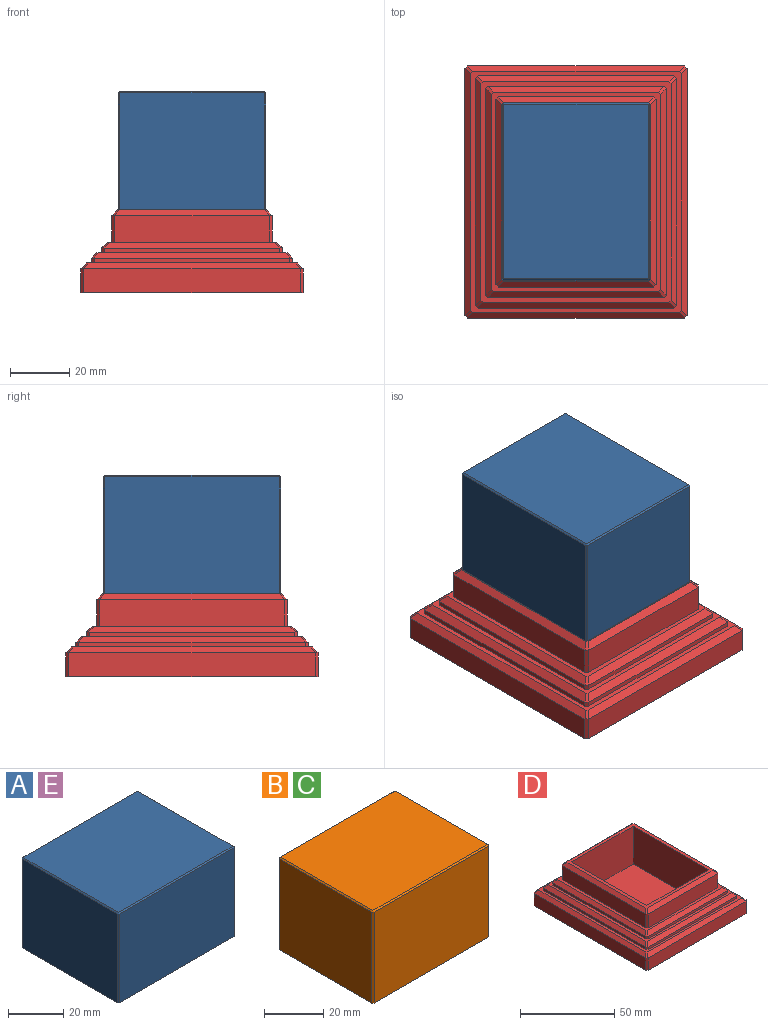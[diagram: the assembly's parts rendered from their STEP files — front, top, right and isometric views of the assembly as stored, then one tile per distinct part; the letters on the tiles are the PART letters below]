
ASSEMBLY  parts=5 mates=4
PART A: 23 faces, bbox 60x50x40 mm
  f0: plane 60x50mm, normal (0,0,-1), area 423.5mm2, adj f1,f2,f3,f4,f6,f7,f8,f9
  f1: plane 49x39.5mm, normal (1,0,0), area 1935.5mm2, adj f0,f13,f19,f22
  f2: plane 59x39.5mm, normal (0,1,0), area 2330.5mm2, adj f0,f16,f20,f22
  f3: plane 49x39.5mm, normal (-1,0,0), area 1935.5mm2, adj f0,f11,f15,f16
  f4: plane 59x39.5mm, normal (0,-1,0), area 2330.5mm2, adj f0,f11,f13,f14
  f5: plane 59x49mm, normal (0,0,1), area 2891mm2, adj f14,f15,f19,f20
  f6: plane 46x38mm, normal (-1,0,0), area 1748mm2, adj f0,f7,f9,f10
  f7: plane 56x38mm, normal (0,-1,0), area 2128mm2, adj f0,f6,f8,f10
  f8: plane 46x38mm, normal (1,0,0), area 1748mm2, adj f0,f7,f9,f10
  f9: plane 56x38mm, normal (0,1,0), area 2128mm2, adj f0,f6,f8,f10
  f10: plane 56x46mm, normal (0,0,-1), area 2576mm2, adj f6,f7,f8,f9
  f11: plane 39.5x0.5mm, normal (-0.71,-0.71,0), area 27.9mm2, adj f0,f3,f4,f12
  f12: plane 0.5x0.5mm, normal (-0.58,-0.58,0.58), area 0.2mm2, adj f11,f14,f15
  f13: plane 39.5x0.5mm, normal (0.71,-0.71,0), area 27.9mm2, adj f0,f1,f4,f17
  f14: plane 59x0.5mm, normal (0,-0.71,0.71), area 41.7mm2, adj f4,f5,f12,f17
  f15: plane 49x0.5mm, normal (-0.71,0,0.71), area 34.6mm2, adj f3,f5,f12,f18
  f16: plane 39.5x0.5mm, normal (-0.71,0.71,0), area 27.9mm2, adj f0,f2,f3,f18
  f17: plane 0.5x0.5mm, normal (0.58,-0.58,0.58), area 0.2mm2, adj f13,f14,f19
  f18: plane 0.5x0.5mm, normal (-0.58,0.58,0.58), area 0.2mm2, adj f15,f16,f20
  f19: plane 49x0.5mm, normal (0.71,0,0.71), area 34.6mm2, adj f1,f5,f17,f21
  f20: plane 59x0.5mm, normal (0,0.71,0.71), area 41.7mm2, adj f2,f5,f18,f21
  f21: plane 0.5x0.5mm, normal (0.58,0.58,0.58), area 0.2mm2, adj f19,f20,f22
  f22: plane 39.5x0.5mm, normal (0.71,0.71,0), area 27.9mm2, adj f0,f1,f2,f21
PART B: 23 faces, bbox 55.5x45x38 mm
  f0: plane 55.5x45mm, normal (0,0,-1), area 385.5mm2, adj f1,f2,f3,f4,f6,f7,f8,f9
  f1: plane 44x37.5mm, normal (1,0,0), area 1650mm2, adj f0,f11,f13,f14
  f2: plane 54.5x37.5mm, normal (0,1,0), area 2043.7mm2, adj f0,f13,f19,f22
  f3: plane 44x37.5mm, normal (-1,0,0), area 1650mm2, adj f0,f16,f20,f22
  f4: plane 54.5x37.5mm, normal (0,-1,0), area 2043.7mm2, adj f0,f11,f15,f16
  f5: plane 54.5x44mm, normal (0,0,1), area 2398mm2, adj f14,f15,f19,f20
  f6: plane 41x36mm, normal (-1,0,0), area 1476mm2, adj f0,f7,f9,f10
  f7: plane 51.5x36mm, normal (0,-1,0), area 1854mm2, adj f0,f6,f8,f10
  f8: plane 41x36mm, normal (1,0,0), area 1476mm2, adj f0,f7,f9,f10
  f9: plane 51.5x36mm, normal (0,1,0), area 1854mm2, adj f0,f6,f8,f10
  f10: plane 51.5x41mm, normal (0,0,-1), area 2111.5mm2, adj f6,f7,f8,f9
  f11: plane 37.5x0.5mm, normal (0.71,-0.71,0), area 26.5mm2, adj f0,f1,f4,f12
  f12: plane 0.5x0.5mm, normal (0.58,-0.58,0.58), area 0.2mm2, adj f11,f14,f15
  f13: plane 37.5x0.5mm, normal (0.71,0.71,0), area 26.5mm2, adj f0,f1,f2,f17
  f14: plane 44x0.5mm, normal (0.71,0,0.71), area 31.1mm2, adj f1,f5,f12,f17
  f15: plane 54.5x0.5mm, normal (0,-0.71,0.71), area 38.5mm2, adj f4,f5,f12,f18
  f16: plane 37.5x0.5mm, normal (-0.71,-0.71,0), area 26.5mm2, adj f0,f3,f4,f18
  f17: plane 0.5x0.5mm, normal (0.58,0.58,0.58), area 0.2mm2, adj f13,f14,f19
  f18: plane 0.5x0.5mm, normal (-0.58,-0.58,0.58), area 0.2mm2, adj f15,f16,f20
  f19: plane 54.5x0.5mm, normal (0,0.71,0.71), area 38.5mm2, adj f2,f5,f17,f21
  f20: plane 44x0.5mm, normal (-0.71,0,0.71), area 31.1mm2, adj f3,f5,f18,f21
  f21: plane 0.5x0.5mm, normal (-0.58,0.58,0.58), area 0.2mm2, adj f19,f20,f22
  f22: plane 37.5x0.5mm, normal (-0.71,0.71,0), area 26.5mm2, adj f0,f2,f3,f21
PART C: same geometry as B
PART D: 74 faces, bbox 75.2x85.5x28 mm
  f0: plane 46.25x24.5mm, normal (0,-1,0), area 1133.1mm2, adj f1,f2,f24,f25
  f1: plane 56.5x24.5mm, normal (-1,0,0), area 1384.3mm2, adj f0,f3,f24,f25
  f2: plane 56.5x24.5mm, normal (1,0,0), area 1384.3mm2, adj f0,f3,f24,f25
  f3: plane 46.25x24.5mm, normal (0,1,0), area 1133.1mm2, adj f1,f2,f24,f25
  f4: plane 52.25x9mm, normal (0,1,0), area 470.2mm2, adj f17,f26,f50,f58
  f5: plane 59.25x1.5mm, normal (0,1,0), area 88.9mm2, adj f19,f33,f52,f60
  f6: plane 66.25x1.5mm, normal (0,1,0), area 99.4mm2, adj f21,f37,f54,f62
  f7: plane 73.25x8mm, normal (0,1,0), area 586mm2, adj f23,f40,f56,f64
  f8: plane 62.5x9mm, normal (1,0,0), area 562.5mm2, adj f17,f27,f58,f66
  f9: plane 69.5x1.5mm, normal (1,0,0), area 104.3mm2, adj f19,f32,f60,f68
  f10: plane 76.5x1.5mm, normal (1,0,0), area 114.7mm2, adj f21,f36,f62,f70
  f11: plane 83.5x8mm, normal (1,0,0), area 668mm2, adj f23,f38,f64,f72
  f12: plane 62.5x9mm, normal (-1,0,0), area 562.5mm2, adj f17,f28,f42,f50
  f13: plane 69.5x1.5mm, normal (-1,0,0), area 104.3mm2, adj f19,f31,f44,f52
  f14: plane 76.5x1.5mm, normal (-1,0,0), area 114.7mm2, adj f21,f35,f46,f54
  f15: plane 83.5x8mm, normal (-1,0,0), area 668mm2, adj f23,f41,f48,f56
  f16: plane 52.25x9mm, normal (0,-1,0), area 470.2mm2, adj f17,f29,f42,f66
  f17: plane 67.5x57.25mm, normal (0,0,1), area 366.2mm2, adj f4,f8,f12,f16,f30,f31,f32,f33
  f18: plane 59.25x1.5mm, normal (0,-1,0), area 88.9mm2, adj f19,f30,f44,f68
  f19: plane 74.5x64.25mm, normal (0,0,1), area 408.2mm2, adj f5,f9,f13,f18,f34,f35,f36,f37
  f20: plane 66.25x1.5mm, normal (0,-1,0), area 99.4mm2, adj f21,f34,f46,f70
  f21: plane 81.5x71.25mm, normal (0,0,1), area 450.2mm2, adj f6,f10,f14,f20,f38,f39,f40,f41
  f22: plane 73.25x8mm, normal (0,-1,0), area 586mm2, adj f23,f39,f48,f72
  f23: plane 85.5x75.25mm, normal (0,0,-1), area 6431.7mm2, adj f7,f11,f15,f22,f48,f56,f64,f72
  f24: plane 60.5x50.25mm, normal (0,0,1), area 426mm2, adj f0,f1,f2,f3,f26,f27,f28,f29
  f25: plane 56.5x46.25mm, normal (0,0,1), area 2613mm2, adj f0,f1,f2,f3
  f26: plane 52.54x2mm, normal (0,0.71,0.71), area 143.7mm2, adj f4,f24,f50,f51,f58,f59
  f27: plane 62.79x2mm, normal (0.71,0,0.71), area 172.7mm2, adj f8,f24,f58,f59,f66,f67
  f28: plane 62.79x2mm, normal (-0.71,0,0.71), area 172.7mm2, adj f12,f24,f42,f43,f50,f51
  f29: plane 52.54x2mm, normal (0,-0.71,0.71), area 143.7mm2, adj f16,f24,f42,f43,f66,f67
  f30: plane 59.54x2mm, normal (0,-0.71,0.71), area 163.5mm2, adj f17,f18,f44,f45,f68,f69
  f31: plane 69.79x2mm, normal (-0.71,0,0.71), area 192.5mm2, adj f13,f17,f44,f45,f52,f53
  f32: plane 69.79x2mm, normal (0.71,0,0.71), area 192.5mm2, adj f9,f17,f60,f61,f68,f69
  f33: plane 59.54x2mm, normal (0,0.71,0.71), area 163.5mm2, adj f5,f17,f52,f53,f60,f61
  f34: plane 66.54x2mm, normal (0,-0.71,0.71), area 183.3mm2, adj f19,f20,f46,f47,f70,f71
  f35: plane 76.79x2mm, normal (-0.71,0,0.71), area 212.3mm2, adj f14,f19,f46,f47,f54,f55
  f36: plane 76.79x2mm, normal (0.71,0,0.71), area 212.3mm2, adj f10,f19,f62,f63,f70,f71
  f37: plane 66.54x2mm, normal (0,0.71,0.71), area 183.3mm2, adj f6,f19,f54,f55,f62,f63
  f38: plane 83.79x2mm, normal (0.71,0,0.71), area 232.1mm2, adj f11,f21,f64,f65,f72,f73
  f39: plane 73.54x2mm, normal (0,-0.71,0.71), area 203.1mm2, adj f21,f22,f48,f49,f72,f73
  f40: plane 73.54x2mm, normal (0,0.71,0.71), area 203.1mm2, adj f7,f21,f56,f57,f64,f65
  f41: plane 83.79x2mm, normal (-0.71,0,0.71), area 232.1mm2, adj f15,f21,f48,f49,f56,f57
  f42: plane 9.15x1mm, normal (-0.71,-0.71,0), area 12.9mm2, adj f12,f16,f17,f28,f29,f43
  f43: plane 2.56x2.56mm, normal (-0.41,-0.41,0.82), area 3.2mm2, adj f24,f28,f29,f42
  f44: plane 1.65x1mm, normal (-0.71,-0.71,0), area 2.3mm2, adj f13,f18,f19,f30,f31,f45
  f45: plane 2.56x2.56mm, normal (-0.41,-0.41,0.82), area 3.2mm2, adj f17,f30,f31,f44
  f46: plane 1.65x1mm, normal (-0.71,-0.71,0), area 2.3mm2, adj f14,f20,f21,f34,f35,f47
  f47: plane 2.56x2.56mm, normal (-0.41,-0.41,0.82), area 3.2mm2, adj f19,f34,f35,f46
  f48: plane 8.15x1mm, normal (-0.71,-0.71,0), area 11.5mm2, adj f15,f22,f23,f39,f41,f49
  f49: plane 2.56x2.56mm, normal (-0.41,-0.41,0.82), area 3.2mm2, adj f21,f39,f41,f48
  f50: plane 9.15x1mm, normal (-0.71,0.71,0), area 12.9mm2, adj f4,f12,f17,f26,f28,f51
  f51: plane 2.56x2.56mm, normal (-0.41,0.41,0.82), area 3.2mm2, adj f24,f26,f28,f50
  f52: plane 1.65x1mm, normal (-0.71,0.71,0), area 2.3mm2, adj f5,f13,f19,f31,f33,f53
  f53: plane 2.56x2.56mm, normal (-0.41,0.41,0.82), area 3.2mm2, adj f17,f31,f33,f52
  f54: plane 1.65x1mm, normal (-0.71,0.71,0), area 2.3mm2, adj f6,f14,f21,f35,f37,f55
  f55: plane 2.56x2.56mm, normal (-0.41,0.41,0.82), area 3.2mm2, adj f19,f35,f37,f54
  f56: plane 8.15x1mm, normal (-0.71,0.71,0), area 11.5mm2, adj f7,f15,f23,f40,f41,f57
  f57: plane 2.56x2.56mm, normal (-0.41,0.41,0.82), area 3.2mm2, adj f21,f40,f41,f56
  f58: plane 9.15x1mm, normal (0.71,0.71,0), area 12.9mm2, adj f4,f8,f17,f26,f27,f59
  f59: plane 2.56x2.56mm, normal (0.41,0.41,0.82), area 3.2mm2, adj f24,f26,f27,f58
  f60: plane 1.65x1mm, normal (0.71,0.71,0), area 2.3mm2, adj f5,f9,f19,f32,f33,f61
  f61: plane 2.56x2.56mm, normal (0.41,0.41,0.82), area 3.2mm2, adj f17,f32,f33,f60
  f62: plane 1.65x1mm, normal (0.71,0.71,0), area 2.3mm2, adj f6,f10,f21,f36,f37,f63
  f63: plane 2.56x2.56mm, normal (0.41,0.41,0.82), area 3.2mm2, adj f19,f36,f37,f62
  f64: plane 8.15x1mm, normal (0.71,0.71,0), area 11.5mm2, adj f7,f11,f23,f38,f40,f65
  f65: plane 2.56x2.56mm, normal (0.41,0.41,0.82), area 3.2mm2, adj f21,f38,f40,f64
  f66: plane 9.15x1mm, normal (0.71,-0.71,0), area 12.9mm2, adj f8,f16,f17,f27,f29,f67
  f67: plane 2.56x2.56mm, normal (0.41,-0.41,0.82), area 3.2mm2, adj f24,f27,f29,f66
  f68: plane 1.65x1mm, normal (0.71,-0.71,0), area 2.3mm2, adj f9,f18,f19,f30,f32,f69
  f69: plane 2.56x2.56mm, normal (0.41,-0.41,0.82), area 3.2mm2, adj f17,f30,f32,f68
  f70: plane 1.65x1mm, normal (0.71,-0.71,0), area 2.3mm2, adj f10,f20,f21,f34,f36,f71
  f71: plane 2.56x2.56mm, normal (0.41,-0.41,0.82), area 3.2mm2, adj f19,f34,f36,f70
  f72: plane 8.15x1mm, normal (0.71,-0.71,0), area 11.5mm2, adj f11,f22,f23,f38,f39,f73
  f73: plane 2.56x2.56mm, normal (0.41,-0.41,0.82), area 3.2mm2, adj f21,f38,f39,f72
PART E: same geometry as A
PLACE A rot(axis=(0,0,1),90deg) t=(0,0,28)mm
PLACE B rot(axis=(0.71,0,-0.71),180deg) t=(18.25,0,35.5)mm
PLACE C rot(axis=(0.71,0.71,0),180deg) t=(0,0,41.5)mm
PLACE D t=(0,0,28)mm
PLACE E rot(axis=(0,1,0),90deg) t=(-19.75,0,35.5)mm
MATE slider C.f5 <-> D.f25  axis (0,0,-1) through (0,0,3.5)mm
MATE slider E.f1 <-> C.f10  axis (0,0,-1) through (0,0,5.5)mm
MATE slider A.f10 <-> E.f3  axis (0,0,-1) through (0,0,66)mm
MATE slider B.f0 <-> E.f10  axis (1,0,0) through (18.25,0,35.5)mm
